# Revit family: Sanitary_Installation-Systems_hansgrohe_13156000-MyFox-Shower-thermostat-for-exp_
name_source: partatom
category: Plumbing Fixtures
revit_build: Autodesk Revit 2015 (Build: 20140903_1530(x64)
units: mm (PartAtom-declared; Revit-internal decimal feet)

## types (1)
- Chrome 000
    BIMobject category = Installation Systems
    BIMobject category code = sanitary-installation-systems
    BIMobject main category = Sanitary
    BIMobject main category code = sanitary
    Brand url = http://www.hansgrohe-int.com
    Design country = Germany
    Edition number = 1
    GTIN code = https://4011097775111
    IFC Classification = Sanitary Terminal
    Manufacturer country = Germany
    Manufacturer name = hansgrohe
    Material main = Chrome
    Product Guid = ef2f57ec-b4f1-43e0-add5-85761c1ffe53
    Product SKU = 13156000
    Product data url = https://bimobject.com
    Product family = MyFox
    Product group = Shower thermostat
    Product name = 13156000 MyFox Shower thermostat for exposed installation
    QR code = http://bimobject.com
    UNSPSC Code = 301815
    Uniclass 1.4 Code = L721
    Uniclass 1.4 Description = Sanitary equipment
    Uniclass 2015 Code = Pr_40_20_76
    Uniclass 2015 Name = Sanitary accessories

## geometry (parser evidence)
native form markers: Sweep x2
no freeform markers — native parametric forms only
